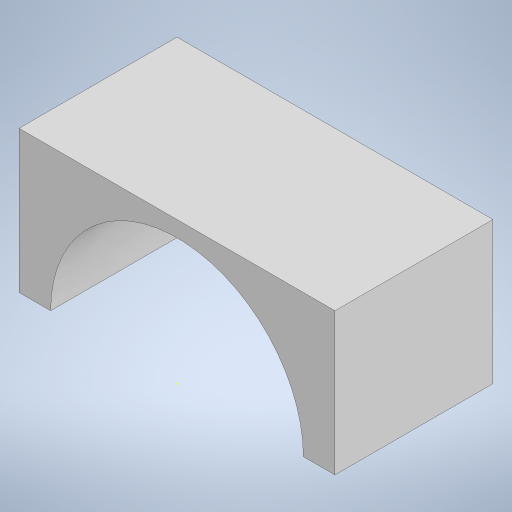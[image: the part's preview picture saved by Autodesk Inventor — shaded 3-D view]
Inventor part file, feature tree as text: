
AUTODESK INVENTOR PART (.ipt)
format: ipt  version: 2023 (Build 270158000, 158)  size: 212,480 bytes
history: native  units: mm
features: sketch x3, extrude x2
ambient origin geometry x8: Origin, YZ Plane, XZ Plane, XY Plane, X Axis, Y Axis, Z Axis, Center Point
bodies: Body1 (feature_tree)
feature tree (5):
  extrude  "Extrusion11"  Depth=45.0mm
  extrude  "Extrusion12"  Depth=50.0mm
  sketch  "Sketch15"  dims[d47=50.0mm d48=0.0mm]
  sketch  "Sketch13"  dims[d42=100.0mm d43=45.0mm]
  sketch  "Sketch14"  dims[d44=50.0mm d45=0.0mm d46=80.0mm]
